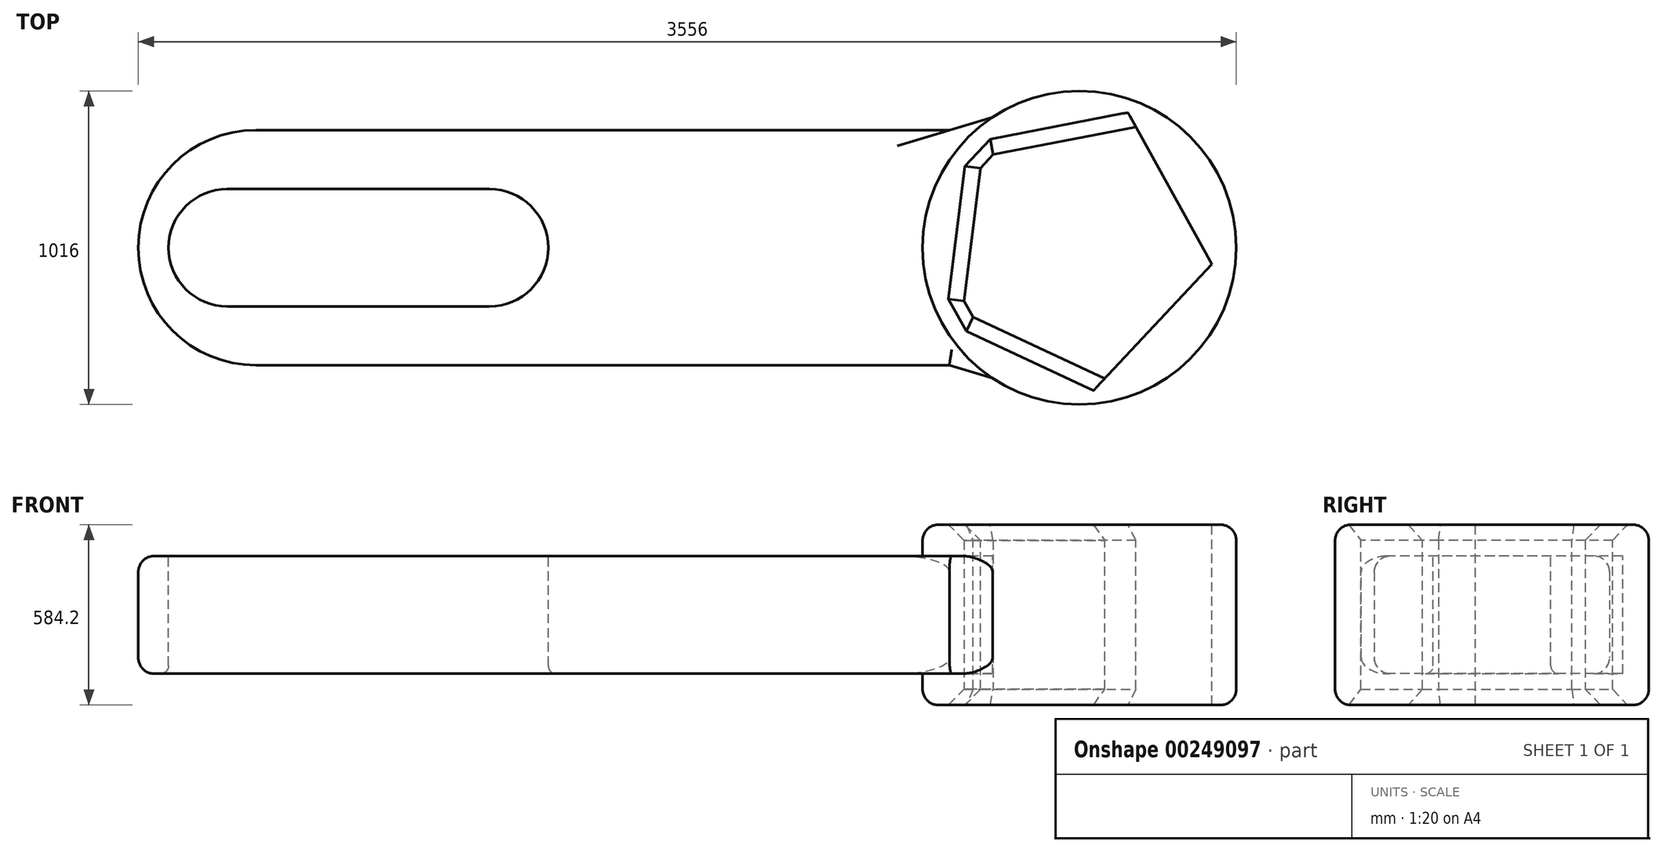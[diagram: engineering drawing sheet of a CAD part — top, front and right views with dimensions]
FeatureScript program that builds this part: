
annotation { "Feature Type Name" : "Feature", "Feature Type Description" : "" }
export const myFeature = defineFeature(function(context is Context, id is Id, definition is map)
    precondition{}
    {
        {
            var Q0;
            Q0=qCreatedBy(makeId("Top.planeOp"),FACE);
            var sketch = newSketch(context, id + "F0", { "sketchPlane" : qUnion([Q0])});
            skLineSegment(sketch, "E0.bottom", {"start": v(-1524, 381) * mm, "end": v(1524, 381) * mm});
            skLineSegment(sketch, "E0.top", {"start": v(-1524, -381) * mm, "end": v(1524, -381) * mm});
            skLineSegment(sketch, "E0.left", {"start": v(-1524, 381) * mm, "end": v(-1524, -381) * mm});
            skLineSegment(sketch, "E0.right", {"start": v(1524, 381) * mm, "end": v(1524, -381) * mm});
            skPoint(sketch, "E0.middle", {"position": v(0, 0) * mm});
            skSolve(sketch);
        }
        {
            var Q0;
            Q0 = qSketchRegion(id + "F0", true);
            var Q1;
            Q1=makeQuery(id+"F0.imprint","IMPRINT",FACE,{"disambiguationData":[TD([[makeQuery(id+"F0.imprint","IMPRINT",EDGE,{"derivedFrom":sQuery(id+"F0.wireOp",EDGE,"E0.bottom")}),-1.0]])]});
            extrude(context, id + "F1", {"entities" : qUnion([Q0, Q1]), "depth" : 381 * mm});
        }
        {
            var Q0;
            Q0=makeQuery(id+"F1.opExtrude","SWEPT_FACE",FACE,{"disambiguationData":[OSD([sQuery(id+"F0.wireOp",EDGE,"E0.right")])]});
            var sketch = newSketch(context, id + "F2", { "sketchPlane" : qUnion([Q0])});
            skLineSegment(sketch, "E1", {"start": v(0, 381) * mm, "end": v(0, 0) * mm, "construction": true});
            skLineSegment(sketch, "E2.bottom", {"start": v(0, 482.6) * mm, "end": v(508, 482.6) * mm});
            skLineSegment(sketch, "E2.top", {"start": v(0, -101.6) * mm, "end": v(508, -101.6) * mm});
            skLineSegment(sketch, "E2.left", {"start": v(0, 482.6) * mm, "end": v(0, -101.6) * mm});
            skLineSegment(sketch, "E2.right", {"start": v(508, 482.6) * mm, "end": v(508, -101.6) * mm});
            skSolve(sketch);
        }
        {
            var Q0;
            {var subQ5=sQuery(id+"F2.wireOp",EDGE,"E2.bottom");Q0=makeQuery(id+"F2.imprint","IMPRINT",FACE,{"disambiguationData":[TD([[makeQuery(id+"F2.imprint","IMPRINT",EDGE,{"derivedFrom":subQ5}),-1.0]])]});}
            var Q1;
            {var subQ1=sQuery(id+"F0.wireOp",EDGE,"E0.right");var subQ6=makeQuery(id+"F1.opExtrude","SWEPT_EDGE",EDGE,{"disambiguationData":[OSD([sQuery(id+"F0.wireOp",EDGE,"E0.bottom"),subQ1])]});Q1=makeQuery(id+"F2.imprint","IMPRINT",FACE,{"disambiguationData":[TD([[makeQuery(id+"F2.imprint","IMPRINT",EDGE,{"derivedFrom":subQ6}),-1.0]])]});}
            var Q2;
            Q2=sQuery(id+"F2.wireOp",EDGE,"E2.left");
            revolve(context, id + "F3", {"operationType" : NewBodyOperationType.ADD, "entities" : qUnion([Q0, Q1]), "axis" : qUnion([Q2]), "revolveType" : RevolveType.FULL});
        }
        {
            var Q0;
            Q0=makeQuery(id+"F3.boolean.opBoolean","INTERSECT",EDGE,{"derivedFrom":[makeQuery(id+"F1.opExtrude","SWEPT_FACE",FACE,{"disambiguationData":[OSD([sQuery(id+"F0.wireOp",EDGE,"E0.top")])]}),makeQuery(id+"F3.opRevolve","SWEPT_FACE",FACE,{"disambiguationData":[OSD([sQuery(id+"F2.wireOp",EDGE,"E2.right")])]})]});
            var Q1;
            Q1=makeQuery(id+"F3.boolean.opBoolean","INTERSECT",EDGE,{"derivedFrom":[makeQuery(id+"F1.opExtrude","SWEPT_FACE",FACE,{"disambiguationData":[OSD([sQuery(id+"F0.wireOp",EDGE,"E0.bottom")])]}),makeQuery(id+"F3.opRevolve","SWEPT_FACE",FACE,{"disambiguationData":[OSD([sQuery(id+"F2.wireOp",EDGE,"E2.right")])]})]});
            chamfer(context, id + "F4", {"entities" : qUnion([Q0, Q1]), "width" : 254 * mm, "tangentPropagation" : true});
        }
        {
            var Q0;
            Q0=makeQuery(id+"F1.opExtrude","SWEPT_EDGE",EDGE,{"disambiguationData":[OSD([sQuery(id+"F0.wireOp",EDGE,"E0.top"),sQuery(id+"F0.wireOp",EDGE,"E0.left")])]});
            var Q1;
            Q1=makeQuery(id+"F1.opExtrude","SWEPT_EDGE",EDGE,{"disambiguationData":[OSD([sQuery(id+"F0.wireOp",EDGE,"E0.bottom"),sQuery(id+"F0.wireOp",EDGE,"E0.left")])]});
            fillet(context, id + "F5", {"entities" : qUnion([Q0, Q1]), "radius" : 381 * mm, "tangentPropagation" : true, "allowEdgeOverflow" : false});
        }
        {
            var Q0;
            Q0=makeQuery(id+"F1.opExtrude","CAP_FACE",FACE,{"disambiguationData":[OSD([sQuery(id+"F0.wireOp",EDGE,"E0.bottom"),sQuery(id+"F0.wireOp",EDGE,"E0.top"),sQuery(id+"F0.wireOp",EDGE,"E0.left"),sQuery(id+"F0.wireOp",EDGE,"E0.right")])],"isStart":false});
            var sketch = newSketch(context, id + "F6", { "sketchPlane" : qUnion([Q0])});
            skArc(sketch, "E3", {"start": v(-1235.55, 190.5) * mm, "mid": v(-1426.05, 0) * mm, "end": v(-1235.55, -190.5) * mm});
            skArc(sketch, "E4", {"start": v(-386.83, -190.5) * mm, "mid": v(-196.33, 0) * mm, "end": v(-386.83, 190.5) * mm});
            skLineSegment(sketch, "E5", {"start": v(-1235.55, 190.5) * mm, "end": v(-386.83, 190.5) * mm});
            skLineSegment(sketch, "E6", {"start": v(-386.83, -190.5) * mm, "end": v(-1235.55, -190.5) * mm});
            skSolve(sketch);
        }
        {
            var Q0;
            Q0=makeQuery(id+"F6.imprint","IMPRINT",FACE,{"disambiguationData":[TD([[makeQuery(id+"F6.imprint","IMPRINT",EDGE,{"derivedFrom":sQuery(id+"F6.wireOp",EDGE,"E3")}),1.0]])]});
            extrude(context, id + "F7", {"entities" : qUnion([Q0]), "operationType" : NewBodyOperationType.REMOVE, "oppositeDirection" : true, "depth" : 1455.42 * mm});
        }
        {
            var Q0;
            Q0=makeQuery(id+"F3.opRevolve","SWEPT_FACE",FACE,{"disambiguationData":[OSD([sQuery(id+"F2.wireOp",EDGE,"E2.bottom")])]});
            var sketch = newSketch(context, id + "F8", { "sketchPlane" : qUnion([Q0])});
            skCircle(sketch, "E7.cCircle", {"center": v(1524, 0) * mm, "radius": 349.6 * mm, "construction": true});
            skLineSegment(sketch, "E7.0", {"start": v(1952.86, -53.05) * mm, "end": v(1606.07, -424.27) * mm});
            skLineSegment(sketch, "E7.1", {"start": v(1606.07, -424.27) * mm, "end": v(1145.86, -209.16) * mm});
            skLineSegment(sketch, "E7.2", {"start": v(1145.86, -209.16) * mm, "end": v(1208.23, 295) * mm});
            skLineSegment(sketch, "E7.3", {"start": v(1208.23, 295) * mm, "end": v(1706.98, 391.48) * mm});
            skLineSegment(sketch, "E7.4", {"start": v(1706.98, 391.48) * mm, "end": v(1952.86, -53.05) * mm});
            skPoint(sketch, "E7.0.midPoint", {"position": v(1779.47, -238.66) * mm});
            skSolve(sketch);
        }
        {
            var Q0;
            Q0=makeQuery(id+"F8.imprint","IMPRINT",FACE,{"disambiguationData":[TD([[makeQuery(id+"F8.imprint","IMPRINT",EDGE,{"derivedFrom":sQuery(id+"F8.wireOp",EDGE,"E7.0")}),-1.0]])]});
            extrude(context, id + "F9", {"entities" : qUnion([Q0]), "operationType" : NewBodyOperationType.REMOVE, "oppositeDirection" : true, "depth" : 769.62 * mm});
        }
        {
            var Q0;
            Q0=makeQuery(id+"F3.opRevolve","SWEPT_EDGE",EDGE,{"disambiguationData":[OSD([sQuery(id+"F2.wireOp",EDGE,"E2.bottom"),sQuery(id+"F2.wireOp",EDGE,"E2.right")])]});
            var Q1;
            Q1=makeQuery(id+"F3.opRevolve","SWEPT_EDGE",EDGE,{"disambiguationData":[OSD([sQuery(id+"F2.wireOp",EDGE,"E2.top"),sQuery(id+"F2.wireOp",EDGE,"E2.right")])]});
            var Q2;
            Q2=makeQuery(id+"F1.opExtrude","CAP_EDGE",EDGE,{"disambiguationData":[OSD([sQuery(id+"F0.wireOp",EDGE,"E0.top")])],"isStart":false});
            var Q3;
            {var subQ0=sQuery(id+"F0.wireOp",EDGE,"E0.left");var subQ1=sQuery(id+"F0.wireOp",EDGE,"E0.bottom");Q3=makeQuery(id+"F5.opFillet","BLEND_EDGE",EDGE,{"blendedFrom":[makeQuery(id+"F1.opExtrude","SWEPT_EDGE",EDGE,{"disambiguationData":[OSD([subQ1,subQ0])]}),makeQuery(id+"F1.opExtrude","CAP_FACE",FACE,{"disambiguationData":[OSD([subQ1,sQuery(id+"F0.wireOp",EDGE,"E0.top"),subQ0,sQuery(id+"F0.wireOp",EDGE,"E0.right")])],"isStart":true})],"blendedInto":[makeQuery(id+"F1.opExtrude","CAP_FACE",FACE,{"disambiguationData":[OSD([subQ1,sQuery(id+"F0.wireOp",EDGE,"E0.top"),subQ0,sQuery(id+"F0.wireOp",EDGE,"E0.right")])],"isStart":true})]});}
            var Q4;
            {var subQ0=sQuery(id+"F0.wireOp",EDGE,"E0.top");Q4=makeQuery(id+"F4.opChamfer","BLEND_EDGE",EDGE,{"blendedFrom":[makeQuery(id+"F3.boolean.opBoolean","INTERSECT",EDGE,{"derivedFrom":[makeQuery(id+"F1.opExtrude","SWEPT_FACE",FACE,{"disambiguationData":[OSD([subQ0])]}),makeQuery(id+"F3.opRevolve","SWEPT_FACE",FACE,{"disambiguationData":[OSD([sQuery(id+"F2.wireOp",EDGE,"E2.right")])]})]}),makeQuery(id+"F1.opExtrude","CAP_FACE",FACE,{"disambiguationData":[OSD([sQuery(id+"F0.wireOp",EDGE,"E0.bottom"),subQ0,sQuery(id+"F0.wireOp",EDGE,"E0.left"),sQuery(id+"F0.wireOp",EDGE,"E0.right")])],"isStart":true})],"blendedInto":[makeQuery(id+"F1.opExtrude","CAP_FACE",FACE,{"disambiguationData":[OSD([sQuery(id+"F0.wireOp",EDGE,"E0.bottom"),subQ0,sQuery(id+"F0.wireOp",EDGE,"E0.left"),sQuery(id+"F0.wireOp",EDGE,"E0.right")])],"isStart":true})]});}
            var Q5;
            {var subQ0=sQuery(id+"F0.wireOp",EDGE,"E0.top");Q5=makeQuery(id+"F4.opChamfer","BLEND_EDGE",EDGE,{"blendedFrom":[makeQuery(id+"F3.boolean.opBoolean","INTERSECT",EDGE,{"derivedFrom":[makeQuery(id+"F1.opExtrude","SWEPT_FACE",FACE,{"disambiguationData":[OSD([subQ0])]}),makeQuery(id+"F3.opRevolve","SWEPT_FACE",FACE,{"disambiguationData":[OSD([sQuery(id+"F2.wireOp",EDGE,"E2.right")])]})]}),makeQuery(id+"F1.opExtrude","CAP_FACE",FACE,{"disambiguationData":[OSD([sQuery(id+"F0.wireOp",EDGE,"E0.bottom"),subQ0,sQuery(id+"F0.wireOp",EDGE,"E0.left"),sQuery(id+"F0.wireOp",EDGE,"E0.right")])],"isStart":false})],"blendedInto":[makeQuery(id+"F1.opExtrude","CAP_FACE",FACE,{"disambiguationData":[OSD([sQuery(id+"F0.wireOp",EDGE,"E0.bottom"),subQ0,sQuery(id+"F0.wireOp",EDGE,"E0.left"),sQuery(id+"F0.wireOp",EDGE,"E0.right")])],"isStart":false})]});}
            fillet(context, id + "F10", {"entities" : qUnion([Q0, Q1, Q2, Q3, Q4, Q5]), "radius" : 50.8 * mm, "tangentPropagation" : true, "allowEdgeOverflow" : false});
        }
        {
            var Q0;
            Q0=makeQuery(id+"F9.boolean.opBoolean","COPY",FACE,{"derivedFrom":makeQuery(id+"F9.opExtrude","SWEPT_FACE",FACE,{"disambiguationData":[OSD([sQuery(id+"F8.wireOp",EDGE,"E7.2")])]})});
            var Q1;
            Q1=makeQuery(id+"F9.boolean.opBoolean","COPY",EDGE,{"derivedFrom":makeQuery(id+"F9.opExtrude","CAP_EDGE",EDGE,{"disambiguationData":[OSD([sQuery(id+"F8.wireOp",EDGE,"E7.2")])],"isStart":true})});
            var Q2;
            Q2=makeQuery(id+"F9.boolean.opBoolean","COPY",EDGE,{"derivedFrom":makeQuery(id+"F9.opExtrude","CAP_EDGE",EDGE,{"disambiguationData":[OSD([sQuery(id+"F8.wireOp",EDGE,"E7.3")])],"isStart":true})});
            chamfer(context, id + "F11", {"entities" : qUnion([Q0, Q1, Q2]), "width" : 50.8 * mm, "tangentPropagation" : true});
        }
        {
            var Q0;
            Q0=makeQuery(id+"F7.boolean.opBoolean","COPY",EDGE,{"derivedFrom":makeQuery(id+"F7.opExtrude","CAP_EDGE",EDGE,{"disambiguationData":[OSD([sQuery(id+"F6.wireOp",EDGE,"E6")])],"isStart":true})});
            var Q1;
            Q1=makeQuery(id+"F7.boolean.opBoolean","COPY",EDGE,{"derivedFrom":makeQuery(id+"F7.opExtrude","CAP_EDGE",EDGE,{"disambiguationData":[OSD([sQuery(id+"F6.wireOp",EDGE,"E3")])],"isStart":true})});
            var Q2;
            Q2=makeQuery(id+"F7.boolean.opBoolean","INTERSECT",EDGE,{"derivedFrom":[makeQuery(id+"F1.opExtrude","CAP_FACE",FACE,{"disambiguationData":[OSD([sQuery(id+"F0.wireOp",EDGE,"E0.bottom"),sQuery(id+"F0.wireOp",EDGE,"E0.top"),sQuery(id+"F0.wireOp",EDGE,"E0.left"),sQuery(id+"F0.wireOp",EDGE,"E0.right")])],"isStart":true}),makeQuery(id+"F7.opExtrude","SWEPT_FACE",FACE,{"disambiguationData":[OSD([sQuery(id+"F6.wireOp",EDGE,"E3")])]})]});
            fillet(context, id + "F12", {"entities" : qUnion([Q0, Q1, Q2]), "radius" : 25.4 * mm, "tangentPropagation" : true, "allowEdgeOverflow" : false});
        }
    });
